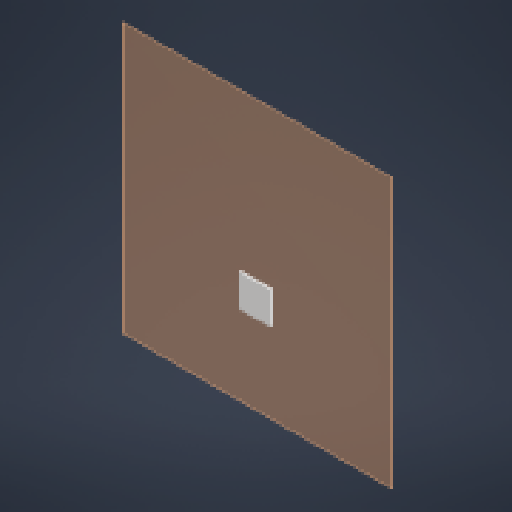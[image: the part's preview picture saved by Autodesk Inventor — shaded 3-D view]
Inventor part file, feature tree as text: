
AUTODESK INVENTOR PART (.ipt)
format: ipt  version: 2023.1 (Build 271208000, 208)  size: 116,224 bytes
history: native  units: mm
features: other x3, plane x2, extrude x1, sketch x1
ambient origin geometry x8: Origin, YZ Plane, XZ Plane, XY Plane, X Axis, Y Axis, Z Axis, Center Point
bodies: Solid1 (feature_tree)
feature tree (7):
  plane  "Work Plane1"
  plane  "Work Plane2"
  extrude  "Extrusion1"  Depth=38.9mm
  sketch  "Sketch1"  dims[d3=70.0mm d4=38.9mm d5=38.9mm d6=3.0mm d7=0.0mm]
  parser-record x1  (decoder bookkeeping rows leaked as tree rows — omitted from the tree; the rows remain in map.json)
  other  "Beau4tClock.iam"
  other  "Clock:1"
note: 1 file-system path scrubbed to <path> (originals preserved in map.json)
